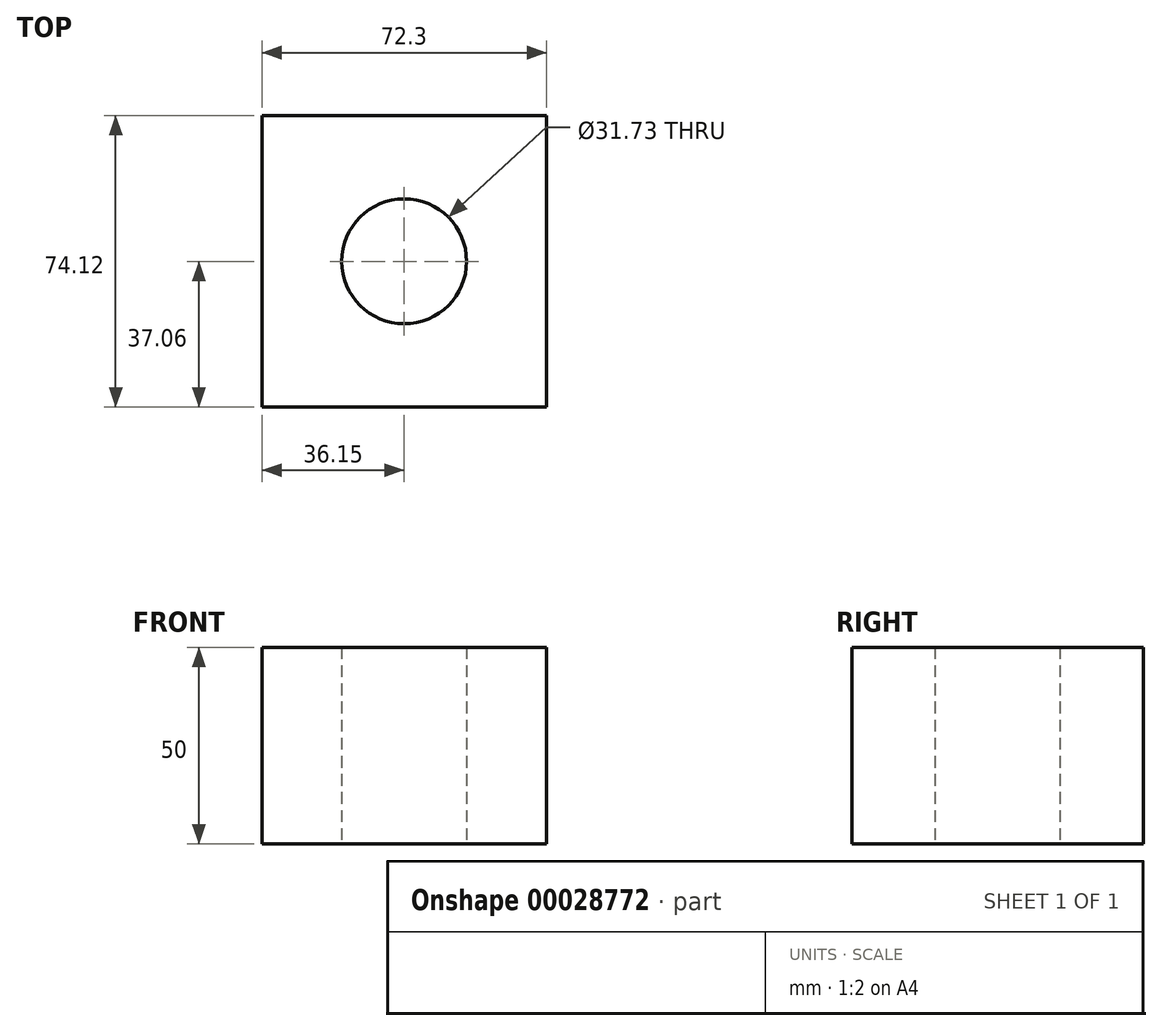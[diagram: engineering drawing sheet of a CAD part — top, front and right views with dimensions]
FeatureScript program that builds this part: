
annotation { "Feature Type Name" : "Feature", "Feature Type Description" : "" }
export const myFeature = defineFeature(function(context is Context, id is Id, definition is map)
    precondition{}
    {
        {
            var Q0;
            Q0=qCreatedBy(makeId("Top.planeOp"),FACE);
            var sketch = newSketch(context, id + "F0", { "sketchPlane" : qUnion([Q0])});
            skLineSegment(sketch, "E0.rect.bottom", {"start": v(36.15, -37.06) * mm, "end": v(-36.15, -37.06) * mm});
            skLineSegment(sketch, "E0.rect.top", {"start": v(36.15, 37.06) * mm, "end": v(-36.15, 37.06) * mm});
            skLineSegment(sketch, "E0.rect.left", {"start": v(36.15, -37.06) * mm, "end": v(36.15, 37.06) * mm});
            skLineSegment(sketch, "E0.rect.right", {"start": v(-36.15, -37.06) * mm, "end": v(-36.15, 37.06) * mm});
            skPoint(sketch, "E0.rect.middle", {"position": v(0, 0) * mm});
            skCircle(sketch, "E1", {"center": v(0, 0) * mm, "radius": 15.86 * mm});
            skSolve(sketch);
        }
        {
            var Q0;
            Q0 = qSketchRegion(id + "F0", true);
            extrude(context, id + "F1", {"entities" : qUnion([Q0]), "depth" : 25 * mm});
        }
        {
            var Q0;
            Q0 = qSketchRegion(id + "F0", true);
            extrude(context, id + "F2", {"entities" : qUnion([Q0]), "operationType" : NewBodyOperationType.ADD, "oppositeDirection" : true, "depth" : 25 * mm});
        }
    });
